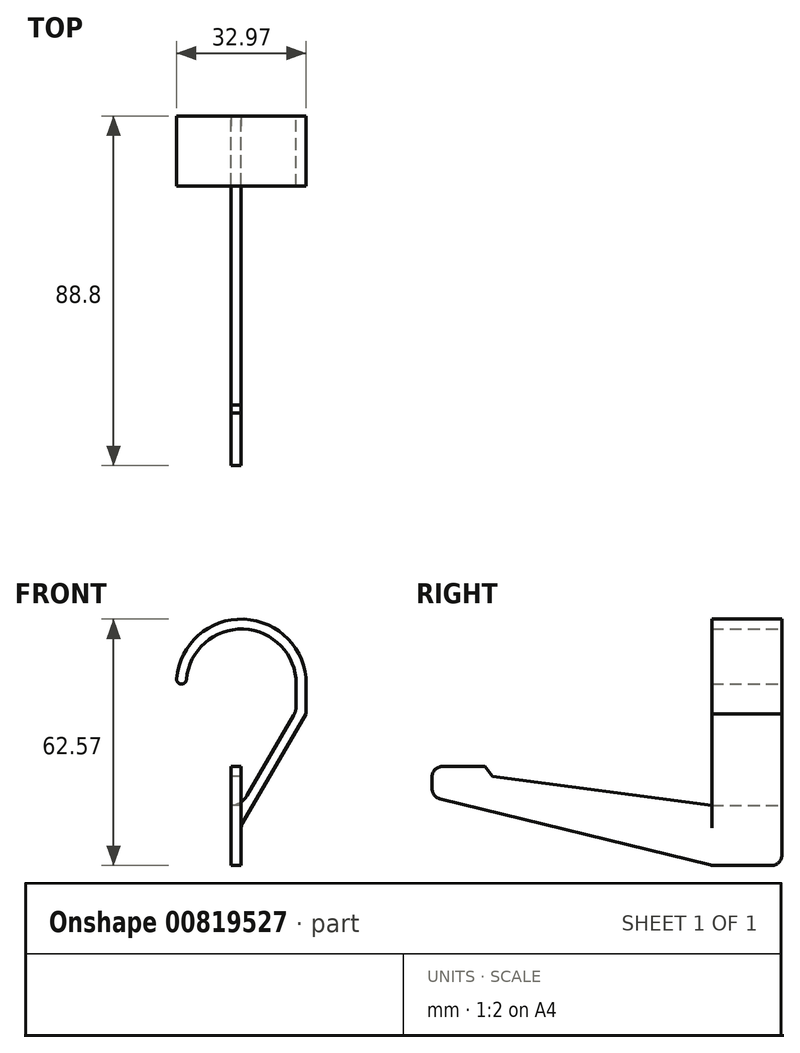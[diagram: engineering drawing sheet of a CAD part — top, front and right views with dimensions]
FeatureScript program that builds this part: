
annotation { "Feature Type Name" : "Feature", "Feature Type Description" : "" }
export const myFeature = defineFeature(function(context is Context, id is Id, definition is map)
    precondition{}
    {
        {
            var Q0;
            Q0=qCreatedBy(makeId("Front.planeOp"),FACE);
            var sketch = newSketch(context, id + "F0", { "sketchPlane" : qUnion([Q0])});
            skArc(sketch, "E0", {"start": v(13.97, 0) * mm, "mid": v(0, 13.97) * mm, "end": v(-13.97, 0) * mm});
            skPoint(sketch, "E1.start.orphan", {"position": v(-29.6, 0) * mm});
            skArc(sketch, "E2.0", {"start": v(16.51, 0) * mm, "mid": v(0, 16.51) * mm, "end": v(-16.51, 0) * mm});
            skLineSegment(sketch, "E3", {"start": v(13.97, 0) * mm, "end": v(13.97, -6.83) * mm});
            skLineSegment(sketch, "E4", {"start": v(13.97, -6.83) * mm, "end": v(0, -30.82) * mm});
            skLineSegment(sketch, "E5", {"start": v(16.51, 0) * mm, "end": v(16.51, -7.52) * mm});
            skLineSegment(sketch, "E6", {"start": v(16.5, -7.52) * mm, "end": v(0, -35.87) * mm});
            skLineSegment(sketch, "E7", {"start": v(-16.51, 0) * mm, "end": v(-13.97, 0) * mm});
            skLineSegment(sketch, "E8.bottom", {"start": v(0, -30.82) * mm, "end": v(-2.54, -30.82) * mm});
            skLineSegment(sketch, "E8.top", {"start": v(0, -46.06) * mm, "end": v(-2.54, -46.06) * mm});
            skLineSegment(sketch, "E8.left", {"start": v(0, -35.87) * mm, "end": v(0, -46.06) * mm});
            skLineSegment(sketch, "E8.right", {"start": v(-2.54, -30.82) * mm, "end": v(-2.54, -46.06) * mm});
            skSolve(sketch);
        }
        {
            var Q0;
            Q0=makeQuery(id+"F0.imprint","IMPRINT",FACE,{"disambiguationData":[TD([[makeQuery(id+"F0.imprint","IMPRINT",EDGE,{"derivedFrom":sQuery(id+"F0.wireOp",EDGE,"E0")}),-1.0]])]});
            extrude(context, id + "F1", {"entities" : qUnion([Q0]), "depth" : 17.78 * mm, "offsetDistance" : 25.4 * mm});
        }
        {
            var Q0;
            Q0=makeQuery(id+"F1.opExtrude","SWEPT_FACE",FACE,{"disambiguationData":[OSD([sQuery(id+"F0.wireOp",EDGE,"E8.right")])]});
            var sketch = newSketch(context, id + "F2", { "sketchPlane" : qUnion([Q0])});
            skLineSegment(sketch, "E9", {"start": v(17.78, -30.82) * mm, "end": v(73.46, -23.4) * mm});
            skLineSegment(sketch, "E10", {"start": v(73.46, -23.4) * mm, "end": v(75.44, -20.93) * mm});
            skLineSegment(sketch, "E11", {"start": v(75.44, -20.93) * mm, "end": v(88.8, -20.93) * mm});
            skLineSegment(sketch, "E12", {"start": v(88.8, -20.93) * mm, "end": v(88.8, -28.7) * mm});
            skLineSegment(sketch, "E13", {"start": v(88.8, -28.7) * mm, "end": v(17.78, -46.06) * mm});
            skSolve(sketch);
        }
        {
            var Q0;
            Q0=makeQuery(id+"F2.imprint","IMPRINT",FACE,{"disambiguationData":[TD([[makeQuery(id+"F2.imprint","IMPRINT",EDGE,{"derivedFrom":sQuery(id+"F2.wireOp",EDGE,"E9")}),-1.0]])]});
            extrude(context, id + "F3", {"entities" : qUnion([Q0]), "oppositeDirection" : true, "depth" : 2.54 * mm, "offsetDistance" : 25.4 * mm});
        }
        {
            var Q0;
            Q0=makeQuery(id+"F1.opExtrude","SWEPT_EDGE",EDGE,{"disambiguationData":[OSD([sQuery(id+"F0.wireOp",EDGE,"E3"),sQuery(id+"F0.wireOp",EDGE,"E4")])]});
            var Q1;
            Q1=makeQuery(id+"F1.opExtrude","SWEPT_EDGE",EDGE,{"disambiguationData":[OSD([sQuery(id+"F0.wireOp",EDGE,"E4"),sQuery(id+"F0.wireOp",EDGE,"E8.bottom")])]});
            fillet(context, id + "F4", {"entities" : qUnion([Q0, Q1]), "radius" : 5.08 * mm, "tangentPropagation" : true, "allowEdgeOverflow" : false});
        }
        {
            var Q0;
            Q0=makeQuery(id+"F3.opExtrude","SWEPT_BODY",BODY,{"disambiguationData":[OSD([sQuery(id+"F0.wireOp",EDGE,"E8.right"),sQuery(id+"F2.wireOp",EDGE,"E9"),sQuery(id+"F2.wireOp",EDGE,"E10"),sQuery(id+"F2.wireOp",EDGE,"E11"),sQuery(id+"F2.wireOp",EDGE,"E12"),sQuery(id+"F2.wireOp",EDGE,"E13")])]});
            var Q1;
            Q1=makeQuery(id+"F1.opExtrude","SWEPT_BODY",BODY,{"disambiguationData":[OSD([sQuery(id+"F0.wireOp",EDGE,"E0"),sQuery(id+"F0.wireOp",EDGE,"E2.0"),sQuery(id+"F0.wireOp",EDGE,"E3"),sQuery(id+"F0.wireOp",EDGE,"E4"),sQuery(id+"F0.wireOp",EDGE,"E5"),sQuery(id+"F0.wireOp",EDGE,"E6"),sQuery(id+"F0.wireOp",EDGE,"E7"),sQuery(id+"F0.wireOp",EDGE,"E8.bottom"),sQuery(id+"F0.wireOp",EDGE,"E8.top"),sQuery(id+"F0.wireOp",EDGE,"E8.left"),sQuery(id+"F0.wireOp",EDGE,"E8.right")])]});
            booleanBodies(context, id + "F5", {"operationType" : BooleanOperationType.UNION, "tools" : qUnion([Q0, Q1])});
        }
        {
            var Q0;
            Q0=makeQuery(id+"F3.opExtrude","CAP_EDGE",EDGE,{"disambiguationData":[OSD([sQuery(id+"F0.wireOp",EDGE,"E8.right")])],"isStart":false});
            var Q1;
            Q1=makeQuery(id+"F1.opExtrude","SWEPT_EDGE",EDGE,{"disambiguationData":[OSD([sQuery(id+"F0.wireOp",EDGE,"E6"),sQuery(id+"F0.wireOp",EDGE,"E8.left")])]});
            fillet(context, id + "F6", {"entities" : qUnion([Q0, Q1]), "radius" : 2.54 * mm, "tangentPropagation" : true, "allowEdgeOverflow" : false});
        }
        {
            var Q0;
            Q0=makeQuery(id+"F1.opExtrude","SWEPT_EDGE",EDGE,{"disambiguationData":[OSD([sQuery(id+"F0.wireOp",EDGE,"E0"),sQuery(id+"F0.wireOp",EDGE,"E7")])]});
            var Q1;
            Q1=makeQuery(id+"F1.opExtrude","SWEPT_EDGE",EDGE,{"disambiguationData":[OSD([sQuery(id+"F0.wireOp",EDGE,"E2.0"),sQuery(id+"F0.wireOp",EDGE,"E7")])]});
            fillet(context, id + "F7", {"entities" : qUnion([Q0, Q1]), "radius" : 1.27 * mm, "tangentPropagation" : true, "allowEdgeOverflow" : false});
        }
        {
            var Q0;
            Q0=makeQuery(id+"F3.opExtrude","SWEPT_EDGE",EDGE,{"disambiguationData":[OSD([sQuery(id+"F2.wireOp",EDGE,"E11"),sQuery(id+"F2.wireOp",EDGE,"E12")])]});
            var Q1;
            Q1=makeQuery(id+"F3.opExtrude","SWEPT_EDGE",EDGE,{"disambiguationData":[OSD([sQuery(id+"F2.wireOp",EDGE,"E12"),sQuery(id+"F2.wireOp",EDGE,"E13")])]});
            fillet(context, id + "F8", {"entities" : qUnion([Q0, Q1]), "radius" : 2.54 * mm, "tangentPropagation" : true, "allowEdgeOverflow" : false});
        }
        {
            var Q0;
            Q0=makeQuery(id+"F1.opExtrude","CAP_EDGE",EDGE,{"disambiguationData":[OSD([sQuery(id+"F0.wireOp",EDGE,"E8.top")])],"isStart":true});
            var Q1;
            {var subQ0=sQuery(id+"F0.wireOp",EDGE,"E8.top");Q1=makeQuery(id+"F5.opBoolean","MERGE",EDGE,{"derivedFrom":[makeQuery(id+"F1.opExtrude","CAP_EDGE",EDGE,{"disambiguationData":[OSD([subQ0])],"isStart":false}),makeQuery(id+"F3.opExtrude","SWEPT_EDGE",EDGE,{"disambiguationData":[OSD([subQ0,sQuery(id+"F0.wireOp",EDGE,"E8.right"),sQuery(id+"F2.wireOp",EDGE,"E13")])]})]});}
            fillet(context, id + "F9", {"entities" : qUnion([Q0, Q1]), "radius" : 2.54 * mm, "tangentPropagation" : true, "allowEdgeOverflow" : false});
        }
    });
